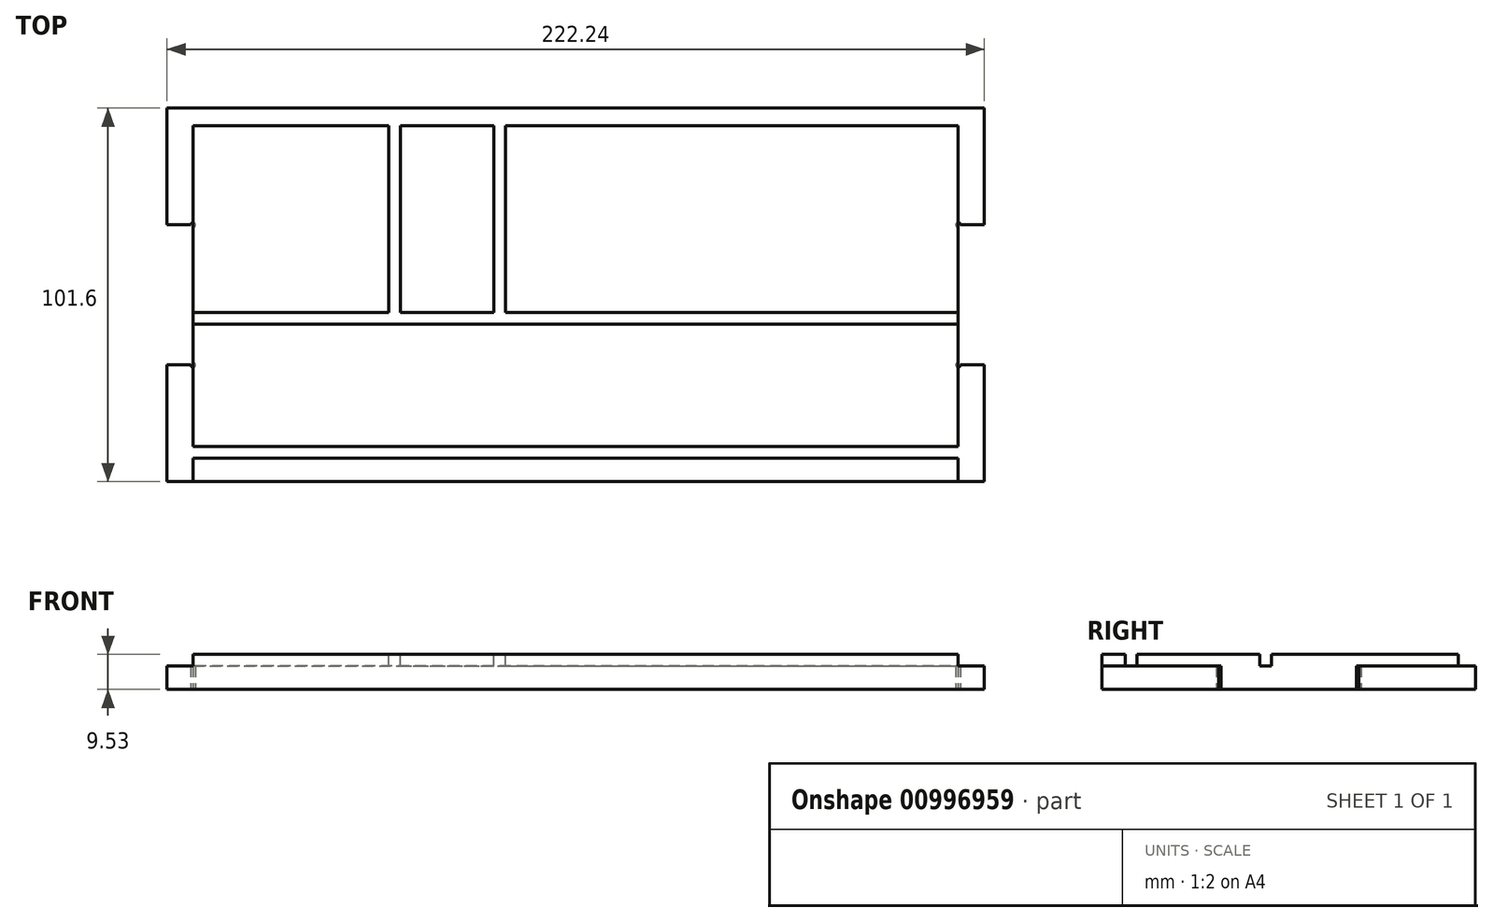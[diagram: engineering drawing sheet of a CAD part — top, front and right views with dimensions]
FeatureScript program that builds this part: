
annotation { "Feature Type Name" : "Feature", "Feature Type Description" : "" }
export const myFeature = defineFeature(function(context is Context, id is Id, definition is map)
    precondition{}
    {
        {
            var Q0;
            Q0=qCreatedBy(makeId("Top.planeOp"),FACE);
            var sketch = newSketch(context, id + "F0", { "sketchPlane" : qUnion([Q0])});
            skLineSegment(sketch, "E0.bottom", {"start": v(111.13, -50.8) * mm, "end": v(-111.12, -50.8) * mm});
            skLineSegment(sketch, "E0.top", {"start": v(111.12, 50.8) * mm, "end": v(-111.13, 50.8) * mm});
            skLineSegment(sketch, "E0.left", {"start": v(111.13, -50.8) * mm, "end": v(111.12, 50.8) * mm});
            skLineSegment(sketch, "E0.right", {"start": v(-111.12, -50.8) * mm, "end": v(-111.13, 50.8) * mm});
            skPoint(sketch, "E0.middle", {"position": v(0, 0) * mm});
            skSolve(sketch);
        }
        {
            var Q0;
            Q0=qSketchRegion(id+"F0",true);
            extrude(context, id + "F1", {"entities" : qUnion([Q0]), "depth" : 9.52 * mm, "offsetDistance" : 25.4 * mm});
        }
        {
            var Q0;
            Q0=makeQuery(id+"F1.opExtrude","CAP_FACE",FACE,{"disambiguationData":[OSD([sQuery(id+"F0.wireOp",EDGE,"E0.bottom"),sQuery(id+"F0.wireOp",EDGE,"E0.top"),sQuery(id+"F0.wireOp",EDGE,"E0.left"),sQuery(id+"F0.wireOp",EDGE,"E0.right")])],"isStart":false});
            var sketch = newSketch(context, id + "F2", { "sketchPlane" : qUnion([Q0])});
            skLineSegment(sketch, "E1.bottom", {"start": v(-111.13, 19.05) * mm, "end": v(-104.01, 19.05) * mm});
            skLineSegment(sketch, "E1.top", {"start": v(-111.13, -19.05) * mm, "end": v(-104.01, -19.05) * mm});
            skLineSegment(sketch, "E1.left", {"start": v(-111.13, 19.05) * mm, "end": v(-111.13, -19.05) * mm});
            skLineSegment(sketch, "E1.right", {"start": v(-104.01, 19.05) * mm, "end": v(-104.01, -19.05) * mm});
            skLineSegment(sketch, "E2.bottom", {"start": v(111.13, 19.05) * mm, "end": v(104.01, 19.05) * mm});
            skLineSegment(sketch, "E2.top", {"start": v(111.13, -19.05) * mm, "end": v(104.01, -19.05) * mm});
            skLineSegment(sketch, "E2.left", {"start": v(111.13, 19.05) * mm, "end": v(111.13, -19.05) * mm});
            skLineSegment(sketch, "E2.right", {"start": v(104.01, 19.05) * mm, "end": v(104.01, -19.05) * mm});
            skLineSegment(sketch, "E3", {"start": v(-111.13, 0) * mm, "end": v(111.12, 0) * mm, "construction": true});
            skSolve(sketch);
        }
        {
            var Q0;
            Q0=qSketchRegion(id+"F2",true);
            extrude(context, id + "F3", {"entities" : qUnion([Q0]), "operationType" : NewBodyOperationType.REMOVE, "endBound" : BoundingType.THROUGH_ALL, "oppositeDirection" : true, "depth" : 25.4 * mm, "offsetDistance" : 25.4 * mm});
        }
        {
            var Q0;
            Q0=makeQuery(id+"F1.opExtrude","CAP_FACE",FACE,{"disambiguationData":[OSD([sQuery(id+"F0.wireOp",EDGE,"E0.bottom"),sQuery(id+"F0.wireOp",EDGE,"E0.top"),sQuery(id+"F0.wireOp",EDGE,"E0.left"),sQuery(id+"F0.wireOp",EDGE,"E0.right")])],"isStart":false});
            var sketch = newSketch(context, id + "F4", { "sketchPlane" : qUnion([Q0])});
            skLineSegment(sketch, "E4", {"start": v(-104.01, 19.05) * mm, "end": v(-104.01, 46.02) * mm});
            skLineSegment(sketch, "E5", {"start": v(-104.01, 46.02) * mm, "end": v(104.01, 46.02) * mm});
            skLineSegment(sketch, "E6", {"start": v(104.01, 46.02) * mm, "end": v(104.01, 19.05) * mm});
            skLineSegment(sketch, "E7", {"start": v(104.01, 19.05) * mm, "end": v(111.13, 19.05) * mm});
            skLineSegment(sketch, "E8", {"start": v(111.12, 19.05) * mm, "end": v(111.12, 50.8) * mm});
            skLineSegment(sketch, "E9", {"start": v(111.12, 50.8) * mm, "end": v(-111.13, 50.8) * mm});
            skLineSegment(sketch, "E10", {"start": v(-111.13, 50.8) * mm, "end": v(-111.13, 19.05) * mm});
            skLineSegment(sketch, "E11", {"start": v(-111.13, 19.05) * mm, "end": v(-104.01, 19.05) * mm});
            skLineSegment(sketch, "E12", {"start": v(-104.01, -19.05) * mm, "end": v(-111.13, -19.05) * mm});
            skLineSegment(sketch, "E13", {"start": v(-111.12, -19.05) * mm, "end": v(-111.12, -50.8) * mm});
            skLineSegment(sketch, "E14", {"start": v(111.13, -50.8) * mm, "end": v(111.13, -19.05) * mm});
            skLineSegment(sketch, "E15", {"start": v(111.13, -19.05) * mm, "end": v(104.01, -19.05) * mm});
            skLineSegment(sketch, "E16", {"start": v(104.01, -19.05) * mm, "end": v(104.01, -50.8) * mm});
            skLineSegment(sketch, "E17", {"start": v(-104.01, -50.8) * mm, "end": v(-104.01, -19.05) * mm});
            skLineSegment(sketch, "E18", {"start": v(-104.01, -50.8) * mm, "end": v(-111.12, -50.8) * mm});
            skLineSegment(sketch, "E19", {"start": v(104.01, -50.8) * mm, "end": v(111.13, -50.8) * mm});
            skSolve(sketch);
        }
        {
            var Q0;
            Q0=qSketchRegion(id+"F4",true);
            extrude(context, id + "F5", {"entities" : qUnion([Q0]), "operationType" : NewBodyOperationType.REMOVE, "oppositeDirection" : true, "depth" : 3.17 * mm, "offsetDistance" : 25.4 * mm});
        }
        {
            var Q0;
            Q0=makeQuery(id+"F1.opExtrude","CAP_FACE",FACE,{"disambiguationData":[OSD([sQuery(id+"F0.wireOp",EDGE,"E0.bottom"),sQuery(id+"F0.wireOp",EDGE,"E0.top"),sQuery(id+"F0.wireOp",EDGE,"E0.left"),sQuery(id+"F0.wireOp",EDGE,"E0.right")])],"isStart":false});
            var sketch = newSketch(context, id + "F6", { "sketchPlane" : qUnion([Q0])});
            skLineSegment(sketch, "E20.bottom", {"start": v(-104.01, -41.28) * mm, "end": v(104.01, -41.27) * mm});
            skLineSegment(sketch, "E20.top", {"start": v(-104.01, -44.45) * mm, "end": v(104.01, -44.45) * mm});
            skLineSegment(sketch, "E20.left", {"start": v(-104.01, -41.28) * mm, "end": v(-104.01, -44.45) * mm});
            skLineSegment(sketch, "E20.right", {"start": v(104.01, -41.27) * mm, "end": v(104.01, -44.45) * mm});
            skLineSegment(sketch, "E21.bottom", {"start": v(-104.01, -4.78) * mm, "end": v(104.01, -4.78) * mm});
            skLineSegment(sketch, "E21.top", {"start": v(-104.01, -7.95) * mm, "end": v(104.01, -7.95) * mm});
            skLineSegment(sketch, "E21.left", {"start": v(-104.01, -4.78) * mm, "end": v(-104.01, -7.95) * mm});
            skLineSegment(sketch, "E21.right", {"start": v(104.01, -4.78) * mm, "end": v(104.01, -7.95) * mm});
            skLineSegment(sketch, "E22", {"start": v(-50.8, 46.02) * mm, "end": v(-47.63, 46.02) * mm});
            skLineSegment(sketch, "E23", {"start": v(-47.63, 46.02) * mm, "end": v(-47.63, -4.78) * mm});
            skLineSegment(sketch, "E24", {"start": v(-50.8, 46.02) * mm, "end": v(-50.8, -4.78) * mm});
            skLineSegment(sketch, "E25", {"start": v(-22.23, -4.78) * mm, "end": v(-22.23, 46.02) * mm});
            skLineSegment(sketch, "E26", {"start": v(-22.23, 46.02) * mm, "end": v(-19.05, 46.02) * mm});
            skLineSegment(sketch, "E27", {"start": v(-19.05, 46.02) * mm, "end": v(-19.05, -4.78) * mm});
            skSolve(sketch);
        }
        {
            var Q0;
            Q0=qSketchRegion(id+"F6",true);
            extrude(context, id + "F7", {"entities" : qUnion([Q0]), "operationType" : NewBodyOperationType.REMOVE, "oppositeDirection" : true, "depth" : 3.17 * mm, "offsetDistance" : 25.4 * mm});
        }
        {
            var Q0;
            Q0=makeQuery(id+"F1.opExtrude","CAP_FACE",FACE,{"disambiguationData":[OSD([sQuery(id+"F0.wireOp",EDGE,"E0.bottom"),sQuery(id+"F0.wireOp",EDGE,"E0.top"),sQuery(id+"F0.wireOp",EDGE,"E0.left"),sQuery(id+"F0.wireOp",EDGE,"E0.right")])],"isStart":true});
            var sketch = newSketch(context, id + "F8", { "sketchPlane" : qUnion([Q0])});
            skArc(sketch, "E28", {"start": v(104.01, -18.41) * mm, "mid": v(103.56, -19.5) * mm, "end": v(104.65, -19.05) * mm});
            skArc(sketch, "E29", {"start": v(104.01, 18.41) * mm, "mid": v(103.56, 19.5) * mm, "end": v(104.65, 19.05) * mm});
            skArc(sketch, "E30", {"start": v(-104.01, 18.41) * mm, "mid": v(-103.56, 19.5) * mm, "end": v(-104.65, 19.05) * mm});
            skArc(sketch, "E31", {"start": v(-104.01, -18.41) * mm, "mid": v(-103.56, -19.5) * mm, "end": v(-104.65, -19.05) * mm});
            skLineSegment(sketch, "E32", {"start": v(-104.65, 19.05) * mm, "end": v(-104.01, 19.05) * mm});
            skLineSegment(sketch, "E33", {"start": v(-104.01, 19.05) * mm, "end": v(-104.01, 18.41) * mm});
            skLineSegment(sketch, "E34", {"start": v(-104.01, -19.05) * mm, "end": v(-104.65, -19.05) * mm});
            skLineSegment(sketch, "E35", {"start": v(-104.01, -19.05) * mm, "end": v(-104.01, -18.41) * mm});
            skLineSegment(sketch, "E36", {"start": v(104.01, -19.05) * mm, "end": v(104.65, -19.05) * mm});
            skLineSegment(sketch, "E37", {"start": v(104.01, -19.05) * mm, "end": v(104.01, -18.41) * mm});
            skLineSegment(sketch, "E38", {"start": v(104.01, 19.05) * mm, "end": v(104.01, 18.41) * mm});
            skLineSegment(sketch, "E39", {"start": v(104.01, 19.05) * mm, "end": v(104.65, 19.05) * mm});
            skSolve(sketch);
        }
        {
            var Q0;
            Q0=qSketchRegion(id+"F8",true);
            var Q1;
            Q1=makeQuery(id+"F7.boolean.opBoolean","MERGE",FACE,{"derivedFrom":[makeQuery(id+"F5.boolean.opBoolean","COPY",FACE,{"derivedFrom":makeQuery(id+"F5.opExtrude","CAP_FACE",FACE,{"disambiguationData":[OSD([sQuery(id+"F4.wireOp",EDGE,"E12"),sQuery(id+"F4.wireOp",EDGE,"E13"),sQuery(id+"F4.wireOp",EDGE,"E17"),sQuery(id+"F4.wireOp",EDGE,"E18")])],"isStart":false})}),makeQuery(id+"F5.boolean.opBoolean","COPY",FACE,{"derivedFrom":makeQuery(id+"F5.opExtrude","CAP_FACE",FACE,{"disambiguationData":[OSD([sQuery(id+"F4.wireOp",EDGE,"E14"),sQuery(id+"F4.wireOp",EDGE,"E15"),sQuery(id+"F4.wireOp",EDGE,"E16"),sQuery(id+"F4.wireOp",EDGE,"E19")])],"isStart":false})})],"fromTools":[makeQuery(id+"F7.opExtrude","CAP_FACE",FACE,{"disambiguationData":[OSD([sQuery(id+"F6.wireOp",EDGE,"E20.bottom"),sQuery(id+"F6.wireOp",EDGE,"E20.top"),sQuery(id+"F6.wireOp",EDGE,"E20.left"),sQuery(id+"F6.wireOp",EDGE,"E20.right")])],"isStart":false})]});
            extrude(context, id + "F9", {"entities" : qUnion([Q0]), "operationType" : NewBodyOperationType.REMOVE, "endBound" : BoundingType.UP_TO_SURFACE, "oppositeDirection" : true, "depth" : 25.4 * mm, "endBoundEntityFace" : qUnion([Q1]), "offsetDistance" : 25.4 * mm});
        }
    });
